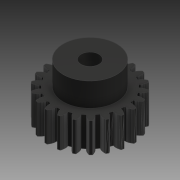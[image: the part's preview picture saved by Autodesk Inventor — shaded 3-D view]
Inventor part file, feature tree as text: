
AUTODESK INVENTOR PART (.ipt)
format: ipt  version: 2018 (Build 220112000, 112)  size: 1,147,392 bytes
history: native  units: mm
features: other x3, extrude x2, sketch x2
ambient origin geometry x8: Origin, YZ Plane, XZ Plane, XY Plane, X Axis, Y Axis, Z Axis, Center Point
bodies: Body1 (feature_tree)
feature tree (7):
  other  "ソリッド1"
  other  "openjscad"
  other  "メッシュ フィーチャ1"
  extrude  "押し出し1"  Depth=9.0mm
  extrude  "押し出し2"  Depth=4.0mm TaperAngle=0.0deg
  sketch  "スケッチ1"
  sketch  "スケッチ2"
